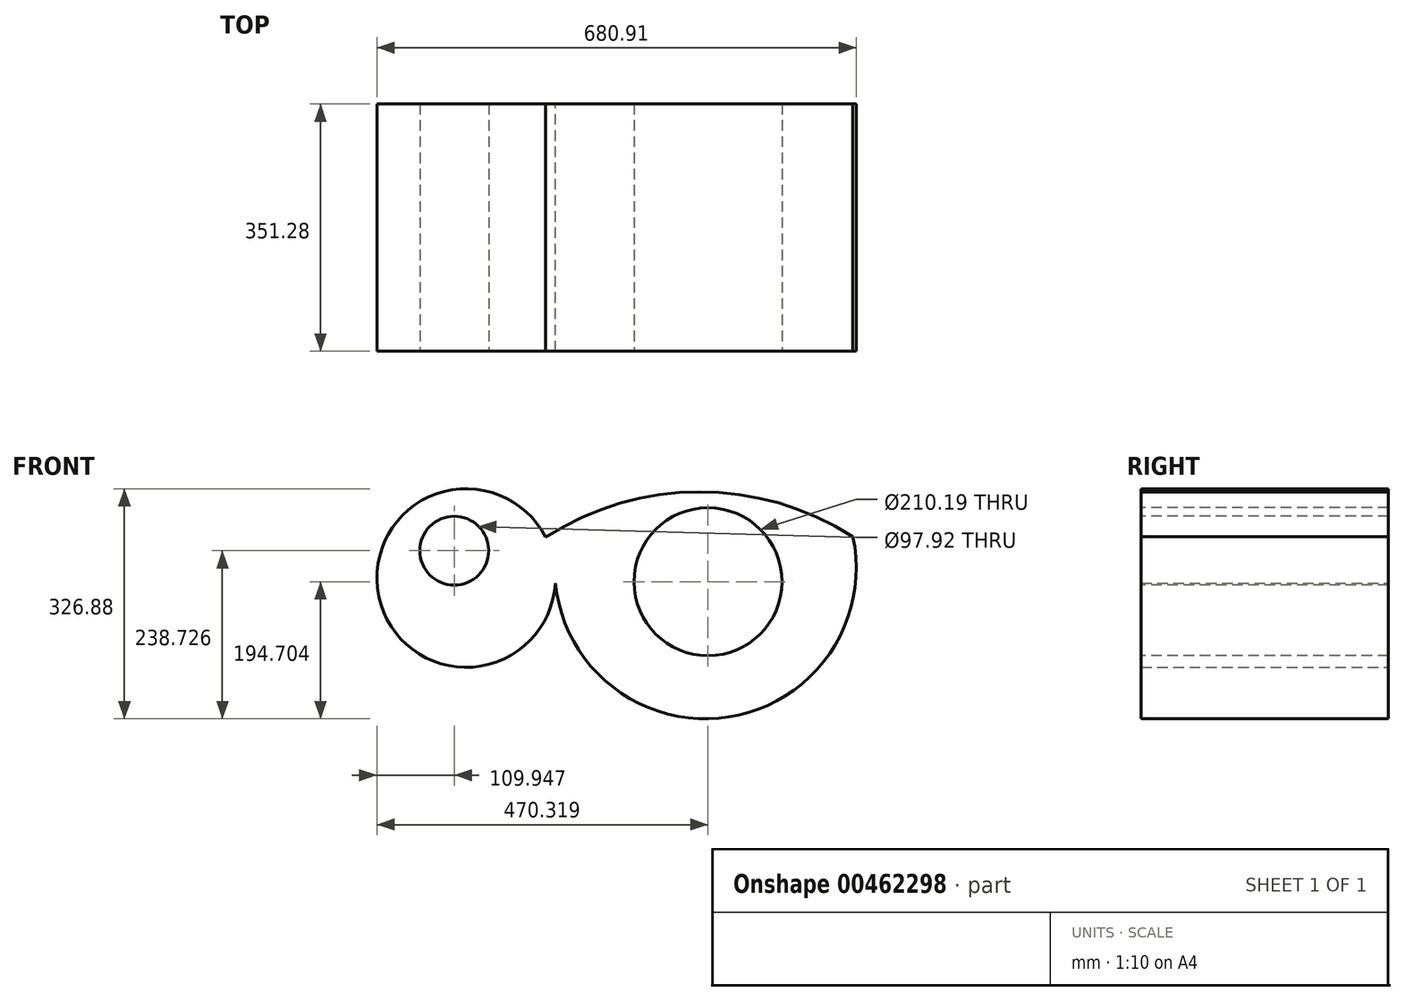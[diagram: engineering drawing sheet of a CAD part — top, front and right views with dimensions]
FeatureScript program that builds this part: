
annotation { "Feature Type Name" : "Feature", "Feature Type Description" : "" }
export const myFeature = defineFeature(function(context is Context, id is Id, definition is map)
    precondition{}
    {
        {
            var Q0;
            Q0=qCreatedBy(makeId("Front.planeOp"),FACE);
            var sketch = newSketch(context, id + "F0", { "sketchPlane" : qUnion([Q0])});
            skArc(sketch, "E0", {"start": v(-44.6, 57.45) * mm, "mid": v(-281.68, -26.57) * mm, "end": v(-30.87, -7.47) * mm});
            skArc(sketch, "E1", {"start": v(-30.87, -7.47) * mm, "mid": v(215.29, -197.78) * mm, "end": v(391.8, 58.46) * mm});
            skArc(sketch, "E2", {"start": v(391.8, 58.46) * mm, "mid": v(173.45, 122.01) * mm, "end": v(-44.6, 57.45) * mm});
            skSolve(sketch);
        }
        {
            var Q0;
            Q0 = qSketchRegion(id + "F0", true);
            extrude(context, id + "F1", {"entities" : qUnion([Q0]), "depth" : 351.28 * mm});
        }
        {
            var Q0;
            Q0=makeQuery(id+"F1.opExtrude","CAP_FACE",FACE,{"disambiguationData":[OSD([sQuery(id+"F0.wireOp",EDGE,"E0"),sQuery(id+"F0.wireOp",EDGE,"E1"),sQuery(id+"F0.wireOp",EDGE,"E2")])],"isStart":false});
            var sketch = newSketch(context, id + "F2", { "sketchPlane" : qUnion([Q0])});
            skCircle(sketch, "E3", {"center": v(-174.47, 38.39) * mm, "radius": 48.96 * mm});
            skCircle(sketch, "E4", {"center": v(185.9, -5.64) * mm, "radius": 105.1 * mm});
            skSolve(sketch);
        }
        {
            var Q0;
            Q0 = qSketchRegion(id + "F2", true);
            extrude(context, id + "F3", {"entities" : qUnion([Q0]), "operationType" : NewBodyOperationType.REMOVE, "oppositeDirection" : true, "depth" : 1374.14 * mm});
        }
    });
